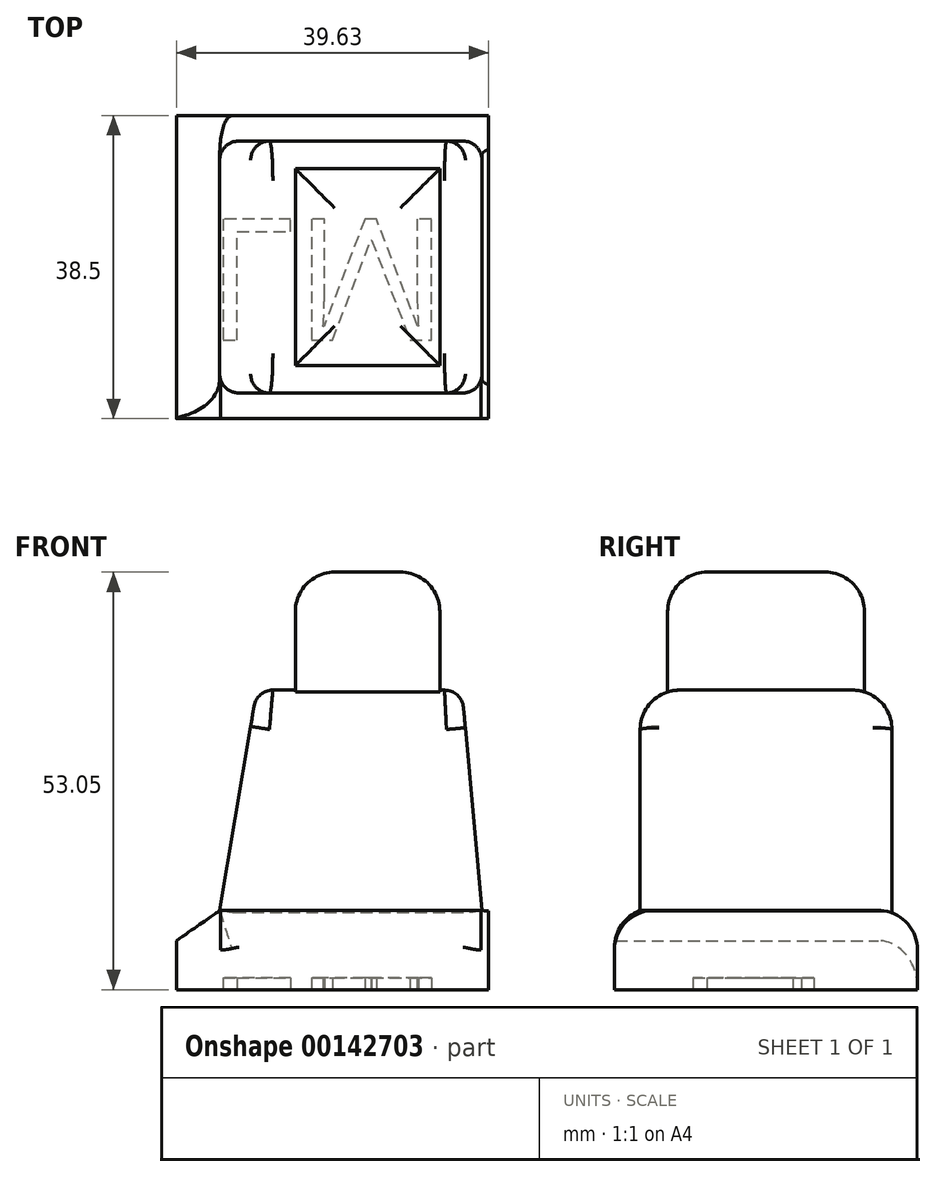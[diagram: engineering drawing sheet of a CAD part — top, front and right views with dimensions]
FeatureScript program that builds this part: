
annotation { "Feature Type Name" : "Feature", "Feature Type Description" : "" }
export const myFeature = defineFeature(function(context is Context, id is Id, definition is map)
    precondition{}
    {
        {
            var Q0;
            Q0=qCreatedBy(makeId("Front.planeOp"),FACE);
            var sketch = newSketch(context, id + "F0", { "sketchPlane" : qUnion([Q0])});
            skLineSegment(sketch, "E0.bottom", {"start": v(-49.86, 38.06) * mm, "end": v(-31.51, 38.06) * mm});
            skLineSegment(sketch, "E0.top", {"start": v(-49.86, 23.06) * mm, "end": v(-31.51, 23.06) * mm});
            skLineSegment(sketch, "E0.left", {"start": v(-49.86, 38.06) * mm, "end": v(-49.86, 23.06) * mm});
            skLineSegment(sketch, "E0.right", {"start": v(-31.51, 38.06) * mm, "end": v(-31.51, 23.06) * mm});
            skLineSegment(sketch, "E1", {"start": v(-31.51, 23.06) * mm, "end": v(-28.7, 23.06) * mm});
            skLineSegment(sketch, "E2", {"start": v(-49.86, 23.06) * mm, "end": v(-54.77, 23.06) * mm});
            skLineSegment(sketch, "E3", {"start": v(-54.77, 23.06) * mm, "end": v(-59.47, -4.94) * mm});
            skLineSegment(sketch, "E4", {"start": v(-28.7, 23.06) * mm, "end": v(-26.16, -4.94) * mm});
            skLineSegment(sketch, "E5", {"start": v(-26.16, -4.94) * mm, "end": v(-59.47, -4.94) * mm});
            skLineSegment(sketch, "E6", {"start": v(-59.47, -4.94) * mm, "end": v(-64.95, -8.76) * mm});
            skLineSegment(sketch, "E7", {"start": v(-64.95, -8.76) * mm, "end": v(-64.95, -14.99) * mm});
            skLineSegment(sketch, "E8", {"start": v(-64.95, -14.99) * mm, "end": v(-25.32, -14.99) * mm});
            skLineSegment(sketch, "E9", {"start": v(-25.32, -14.99) * mm, "end": v(-25.32, -4.99) * mm});
            skLineSegment(sketch, "E10", {"start": v(-26.16, -4.94) * mm, "end": v(-25.32, -4.99) * mm});
            skSolve(sketch);
        }
        {
            var Q0;
            Q0=makeQuery(id+"F0.imprint","IMPRINT",FACE,{"disambiguationData":[TD([[makeQuery(id+"F0.imprint","IMPRINT",EDGE,{"derivedFrom":sQuery(id+"F0.wireOp",EDGE,"E0.bottom")}),-1.0]])]});
            extrude(context, id + "F1", {"entities" : qUnion([Q0]), "depth" : 25 * mm, "symmetric" : true});
        }
        {
            var Q0;
            Q0=makeQuery(id+"F0.imprint","IMPRINT",FACE,{"disambiguationData":[TD([[makeQuery(id+"F0.imprint","IMPRINT",EDGE,{"derivedFrom":sQuery(id+"F0.wireOp",EDGE,"E0.top")}),-1.0]])]});
            extrude(context, id + "F2", {"entities" : qUnion([Q0]), "operationType" : NewBodyOperationType.ADD, "depth" : 32 * mm, "symmetric" : true});
        }
        {
            var Q0;
            Q0=makeQuery(id+"F0.imprint","IMPRINT",FACE,{"disambiguationData":[TD([[makeQuery(id+"F0.imprint","IMPRINT",EDGE,{"derivedFrom":sQuery(id+"F0.wireOp",EDGE,"E5")}),1.0]])]});
            extrude(context, id + "F3", {"entities" : qUnion([Q0]), "operationType" : NewBodyOperationType.ADD, "depth" : 38.5 * mm, "symmetric" : true});
        }
        {
            var Q0;
            Q0=makeQuery(id+"F1.opExtrude","CAP_EDGE",EDGE,{"disambiguationData":[OSD([sQuery(id+"F0.wireOp",EDGE,"E0.bottom")])],"isStart":false});
            var Q1;
            Q1=makeQuery(id+"F1.opExtrude","SWEPT_EDGE",EDGE,{"disambiguationData":[OSD([sQuery(id+"F0.wireOp",EDGE,"E0.bottom"),sQuery(id+"F0.wireOp",EDGE,"E0.left")])]});
            var Q2;
            Q2=makeQuery(id+"F1.opExtrude","CAP_EDGE",EDGE,{"disambiguationData":[OSD([sQuery(id+"F0.wireOp",EDGE,"E0.bottom")])],"isStart":true});
            var Q3;
            Q3=makeQuery(id+"F1.opExtrude","SWEPT_EDGE",EDGE,{"disambiguationData":[OSD([sQuery(id+"F0.wireOp",EDGE,"E0.bottom"),sQuery(id+"F0.wireOp",EDGE,"E0.right")])]});
            fillet(context, id + "F4", {"entities" : qUnion([Q0, Q1, Q2, Q3]), "radius" : 5 * mm, "tangentPropagation" : true, "allowEdgeOverflow" : false});
        }
        {
            var Q0;
            {var subQ1=sQuery(id+"F0.wireOp",EDGE,"E2");var subQ2=sQuery(id+"F0.wireOp",EDGE,"E1");var subQ3=sQuery(id+"F0.wireOp",EDGE,"E0.top");var subQ4=sQuery(id+"F0.wireOp",EDGE,"E0.left");Q0=makeQuery(id+"F2.boolean.opBoolean","SPLIT",EDGE,{"disambiguationData":[TD([makeQuery(id+"F1.opExtrude","SWEPT_FACE",FACE,{"disambiguationData":[OSD([subQ4])]})])],"derivedFrom":makeQuery(id+"F2.opExtrude","CAP_EDGE",EDGE,{"disambiguationData":[OSD([subQ3,subQ2,subQ1])],"isStart":false})});}
            var Q1;
            {var subQ1=sQuery(id+"F0.wireOp",EDGE,"E2");var subQ2=sQuery(id+"F0.wireOp",EDGE,"E1");var subQ3=sQuery(id+"F0.wireOp",EDGE,"E0.top");var subQ4=sQuery(id+"F0.wireOp",EDGE,"E0.right");Q1=makeQuery(id+"F2.boolean.opBoolean","SPLIT",EDGE,{"disambiguationData":[TD([makeQuery(id+"F1.opExtrude","SWEPT_FACE",FACE,{"disambiguationData":[OSD([subQ4])]})])],"derivedFrom":makeQuery(id+"F2.opExtrude","CAP_EDGE",EDGE,{"disambiguationData":[OSD([subQ3,subQ2,subQ1])],"isStart":false})});}
            var Q2;
            {var subQ1=sQuery(id+"F0.wireOp",EDGE,"E2");var subQ2=sQuery(id+"F0.wireOp",EDGE,"E1");var subQ3=sQuery(id+"F0.wireOp",EDGE,"E0.top");var subQ4=sQuery(id+"F0.wireOp",EDGE,"E0.left");Q2=makeQuery(id+"F2.boolean.opBoolean","SPLIT",EDGE,{"disambiguationData":[TD([makeQuery(id+"F1.opExtrude","SWEPT_FACE",FACE,{"disambiguationData":[OSD([subQ4])]})])],"derivedFrom":makeQuery(id+"F2.opExtrude","CAP_EDGE",EDGE,{"disambiguationData":[OSD([subQ3,subQ2,subQ1])],"isStart":true})});}
            var Q3;
            {var subQ1=sQuery(id+"F0.wireOp",EDGE,"E2");var subQ2=sQuery(id+"F0.wireOp",EDGE,"E1");var subQ3=sQuery(id+"F0.wireOp",EDGE,"E0.top");var subQ4=sQuery(id+"F0.wireOp",EDGE,"E0.right");Q3=makeQuery(id+"F2.boolean.opBoolean","SPLIT",EDGE,{"disambiguationData":[TD([makeQuery(id+"F1.opExtrude","SWEPT_FACE",FACE,{"disambiguationData":[OSD([subQ4])]})])],"derivedFrom":makeQuery(id+"F2.opExtrude","CAP_EDGE",EDGE,{"disambiguationData":[OSD([subQ3,subQ2,subQ1])],"isStart":true})});}
            fillet(context, id + "F5", {"entities" : qUnion([Q0, Q1, Q2, Q3]), "radius" : 5 * mm, "tangentPropagation" : true, "allowEdgeOverflow" : false});
        }
        {
            var Q0;
            Q0=makeQuery(id+"F2.opExtrude","CAP_EDGE",EDGE,{"disambiguationData":[OSD([sQuery(id+"F0.wireOp",EDGE,"E4")])],"isStart":false});
            var Q1;
            Q1=makeQuery(id+"F2.opExtrude","CAP_EDGE",EDGE,{"disambiguationData":[OSD([sQuery(id+"F0.wireOp",EDGE,"E3")])],"isStart":false});
            fillet(context, id + "F6", {"entities" : qUnion([Q0, Q1]), "radius" : 2.41 * mm, "tangentPropagation" : true, "allowEdgeOverflow" : false});
        }
        {
            var Q0;
            Q0=makeQuery(id+"F3.opExtrude","CAP_EDGE",EDGE,{"disambiguationData":[OSD([sQuery(id+"F0.wireOp",EDGE,"E5")])],"isStart":false});
            var Q1;
            Q1=makeQuery(id+"F3.opExtrude","CAP_EDGE",EDGE,{"disambiguationData":[OSD([sQuery(id+"F0.wireOp",EDGE,"E5")])],"isStart":true});
            var Q2;
            Q2=makeQuery(id+"F3.opExtrude","CAP_EDGE",EDGE,{"disambiguationData":[OSD([sQuery(id+"F0.wireOp",EDGE,"E6")])],"isStart":true});
            fillet(context, id + "F7", {"entities" : qUnion([Q0, Q1, Q2]), "radius" : 5 * mm, "tangentPropagation" : true, "allowEdgeOverflow" : false});
        }
        {
            var Q0;
            Q0=makeQuery(id+"F3.opExtrude","SWEPT_FACE",FACE,{"disambiguationData":[OSD([sQuery(id+"F0.wireOp",EDGE,"E8")])]});
            var sketch = newSketch(context, id + "F8", { "sketchPlane" : qUnion([Q0])});
            skText(sketch, "E11", { "text": "LM", "fontName": "OpenSans-Regular.ttf"});
            const initialGuessF8  = {"E11": [-0.06114, -0.0061, 1, 0, 0.01552]};
            skSetInitialGuess(sketch, initialGuessF8);
            skSolve(sketch);
        }
        {
            var Q0;
            Q0 = qSketchRegion(id + "F8", true);
            extrude(context, id + "F9", {"entities" : qUnion([Q0]), "operationType" : NewBodyOperationType.REMOVE, "oppositeDirection" : true, "depth" : 1.5 * mm});
        }
    });
